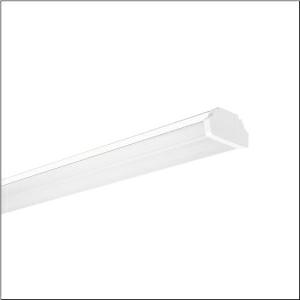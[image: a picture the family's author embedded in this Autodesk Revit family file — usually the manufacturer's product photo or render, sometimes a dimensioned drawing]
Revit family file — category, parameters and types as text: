
# Revit family: modario_31_gen_2_53bm812cv6a5d2_5516
name_source: partatom
category: Lighting Fixtures
units: mm (PartAtom-declared; Revit-internal decimal feet)

## family parameters
Cut with Voids When Loaded = No
Host = Face
Light Source = No
Part Type = Normal
Room Calculation Point = No
Round Connector Dimension = Use Diameter
Shared = No

## types (1)
- --- (1 x LED, 10550 lm, 56.5 W, 6500K)
    Apparent Load = 57 VA
    CIE Flux Codes = 47 80 95 93 100
    Color Rendering = 80
    Color Temperature = 6500K
    Default Elevation = 1800 mm
    Description = Modario 31 Gen.2, luminaire insert, of sheet steel, coil coated, white, length: 1.495mm, width: 81mm, height: 82mm, 5x system unit, system units: 299mm, LED rated luminous flux: 10.550lm, light colour: 865, SDCM (Standard Deviation of Colour Matching)MacAdam ≤ 3 SDCM (initial), control gear: ON/OFF Multilumen, CLOi, with plug, 3-pole, with phase selection, mains connection: 220..240V, AC, 50/60Hz, start of lifetime: 57W, end of service life: 68W, through-wiring accessed according to module size, primary optical cover: cover, of PMMA, light emission: direct distribution, primary light characteristic: symmetric, protection rating (complete): IP20, protection rating (LED compartment): IP50, insulation class (complete): insulation class I (protective earthing), certification: CE, ENEC, VDE, UKCA, impact resistance: IK03, permissible ambient temperature for indoor applications: -35..+40°C, corresponds to IFS (International Featured Standards) requirements for safety and quality in the food industry, reducing of maximum allowable ambient temperature of 5°C with ceiling mounting, IP40 when using the optional accessory 5TP9018, packaging unit: 1 piece
    Height = 92 mm
    Lamp = 1 x LED
    Lamp Light Flux = 10550 lm
    Lamp Power = 56.5 W
    Lamp count = 1
    Length = 1495 mm
    Luminous efficacy = 187 lm/W
    Manufacturer = Siteco
    ModVariant = No
    Model = 53BM812CV6A5D2
    Mounting Place = Ceiling
    Mounting Type = Pendant
    Number of Poles = 1
    OnlyDefault = Yes
    Power Factor = 1
    Product Name = Modario 31 Gen.2
    Product group = luminaire insert | ceiling pendant
    ProductGroupID = 901
    Protection Class = Protection class I
    Protection Degree = IP 20
    RLX_Detail_Level = 1
    RLX_Emergency_Light_Flux = 0 lm
    RLX_Emergency_Type = 0
    RLX_Emergency_Type_DB = No
    RlxData = <blob elided: 39989 chars, md5=2c4c63d3>
    Socket = socket
    Standby Power = 0 W
    System Light Flux = 10550 lm
    System Power = 57 W
    Type Comments = factory setting: luminous flux: 100 % | (A | C | E) | 133 mA
    Type Image = l_1341886.jpg
    URL = http://relux.com
    VarID = @adj_042269
    Voltage = 0 V
    Weight = 0.00 kg
    Width = 81 mm

## geometry (parser evidence)
native form markers: Blend x4, Sweep x11
no freeform markers — native parametric forms only
